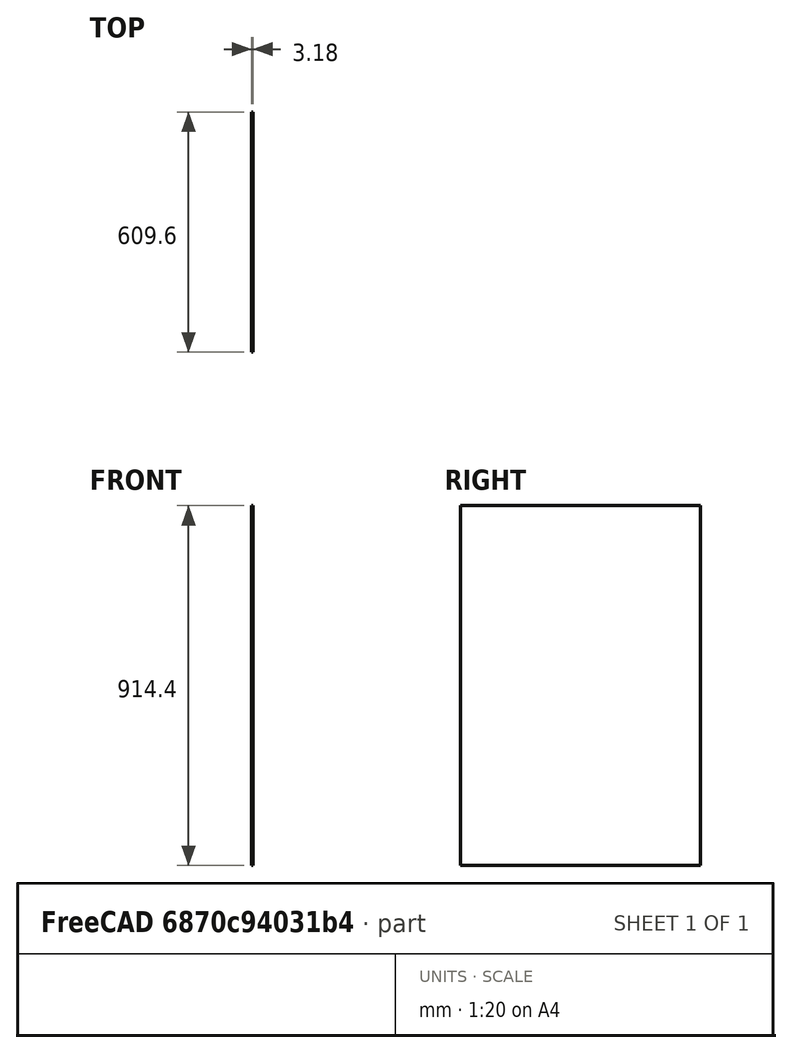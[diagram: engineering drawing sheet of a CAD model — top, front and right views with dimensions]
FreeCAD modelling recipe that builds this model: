
FCSTD DOCUMENT  (FreeCAD 0.17R11141 (Git))
Label: side_panel_24x36in
License: All rights reserved
LicenseURL: http://en.wikipedia.org/wiki/All_rights_reserved
objects: Sketcher::SketchObject×1, PartDesign::Pad×1, PartDesign::Body×1
note: 4 computed .brp shape members not serialized (recipe doc carries the construction recipe); baked Part::Feature solids carry a one-line shape summary decoded from their .brp

FEATURE [Sketcher::SketchObject] Sketch
  MapMode = 5
  Placement = pos=(0,0,0) rot=(0.57735,0.57735,0.57735;2.0944rad)
  Support = -> [YZ_Plane]
  sketch-geometry (6):
    g0: LineSegment StartX=304.8 StartY=457.2 StartZ=0 EndX=-304.8 EndY=457.2 EndZ=0
    g1: LineSegment StartX=-304.8 StartY=457.2 StartZ=0 EndX=-304.8 EndY=-457.2 EndZ=0
    g2: LineSegment StartX=-304.8 StartY=-457.2 StartZ=0 EndX=304.8 EndY=-457.2 EndZ=0
    g3: LineSegment StartX=304.8 StartY=-457.2 StartZ=0 EndX=304.8 EndY=457.2 EndZ=0
    g4: LineSegment [constr] StartX=-304.8 StartY=457.2 StartZ=0 EndX=0 EndY=0 EndZ=0
    g5: LineSegment [constr] StartX=0 StartY=0 StartZ=0 EndX=304.8 EndY=-457.2 EndZ=0
  constraints (16):
    c: Coincident(g0,g1)
    c: Coincident(g1,g2)
    c: Coincident(g2,g3)
    c: Coincident(g3,g0)
    c: Equal(g0,g2)
    c: Vertical(g3)
    c: Horizontal(g2)
    c: Horizontal(g0)
    c: Coincident(g0,g4)
    c: Coincident(g4,g-1)
    c: Coincident(g4,g5)
    c: Coincident(g5,g2)
    c: Equal(g5,g4)
    c: PointOnObject(g2,g4)
    c: DistanceY(g3,g3) = 914.4
    c: DistanceX(g2,g2) = 609.6
FEATURE [PartDesign::Pad] Pad
  Length = 3.175
  Length2 = 100
  Placement = pos=(0,0,0) rot=(0.57735,0.57735,0.57735;2.0944rad)
  Profile = -> Sketch
  Type = 0
FEATURE [PartDesign::Body] Body
  Group = -> [Sketch,Pad]
  Origin = -> BodyOrigin
  Tip = -> Pad
